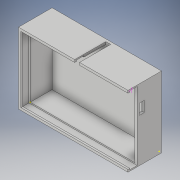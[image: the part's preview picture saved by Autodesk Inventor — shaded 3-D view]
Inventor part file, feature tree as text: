
AUTODESK INVENTOR PART (.ipt)
format: ipt  version: 2018.3 (Build 223284000, 284)  size: 148,992 bytes
history: native  units: in
note: dims shown in document units (in); Inventor stores cm internally (conversion verified against a paired STEP export)
features: sketch x9, extrude x5, shell x1
ambient origin geometry x8: Origin, YZ Plane, XZ Plane, XY Plane, X Axis, Y Axis, Z Axis, Center Point
bodies: Solid1 (feature_tree)
feature tree (15):
  extrude  "Extrusion1"  Depth=2.0866in
  shell  "Shell1"  Thickness=0.9842in
  sketch  "Sketch2"  dims[d4=0.078in d5=0.157in]
  extrude  "Extrusion2"  Depth=0.157in
  extrude  "Extrusion3"  Depth=0.335in TaperAngle=0.0deg
  sketch  "Sketch5"  dims[d14=0.079in d15=0.0in d16=1.0in d17=0.0in]
  sketch  "Sketch6"
  extrude  "Extrusion4"  Depth=3.4252in TaperAngle=0.0deg
  extrude  "Extrusion5"  Depth=1.0in TaperAngle=0.0deg
  sketch  "Sketch9"
  sketch  "Sketch1"  dims[d0=3.307in d1=2.0866in d2=0.9842in d3=0.0in]
  sketch  "Sketch3"  dims[d6=0.335in d7=0.9055in d8=0.0in]
  sketch  "Sketch4"  dims[d9=0.1969in d11=3.4252in d12=0.0in]
  sketch  "Sketch7"
  sketch  "Sketch8"
